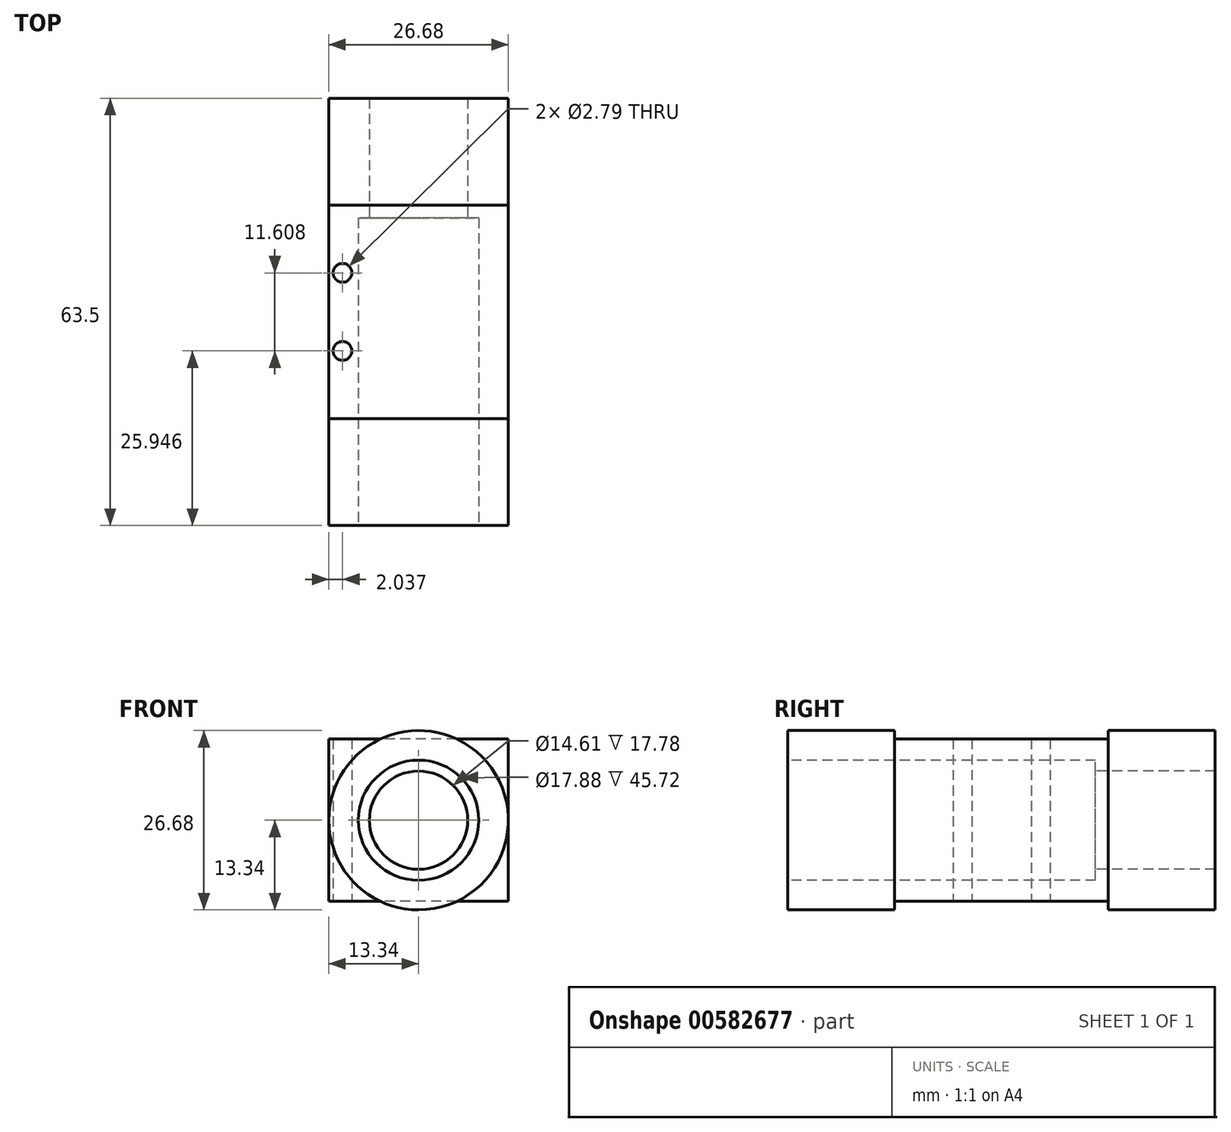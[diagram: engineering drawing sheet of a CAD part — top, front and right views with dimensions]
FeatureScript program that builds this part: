
annotation { "Feature Type Name" : "Feature", "Feature Type Description" : "" }
export const myFeature = defineFeature(function(context is Context, id is Id, definition is map)
    precondition{}
    {
        {
            var Q0;
            Q0=qCreatedBy(makeId("Front.planeOp"),FACE);
            cPlane(context, id + "F0", {"entities" : qUnion([Q0]), "cplaneType" : CPlaneType.OFFSET, "offset" : 31.75 * mm, "width" : 152.4 * mm, "height" : 152.4 * mm});
        }
        {
            var Q0;
            Q0=qCreatedBy(makeId("Front.planeOp"),FACE);
            cPlane(context, id + "F1", {"entities" : qUnion([Q0]), "cplaneType" : CPlaneType.OFFSET, "offset" : 31.75 * mm, "oppositeDirection" : true, "width" : 152.4 * mm, "height" : 152.4 * mm});
        }
        {
            var Q0;
            Q0=qCreatedBy(makeId("Top.planeOp"),FACE);
            cPlane(context, id + "F2", {"entities" : qUnion([Q0]), "cplaneType" : CPlaneType.OFFSET, "offset" : 13.33 * mm, "oppositeDirection" : true, "width" : 152.4 * mm, "height" : 152.4 * mm});
        }
        {
            var Q0;
            Q0=qCreatedBy(makeId("Front.planeOp"),FACE);
            cPlane(context, id + "F3", {"entities" : qUnion([Q0]), "cplaneType" : CPlaneType.OFFSET, "offset" : 15.88 * mm, "width" : 152.4 * mm, "height" : 152.4 * mm});
        }
        {
            var Q0;
            Q0=qCreatedBy(makeId("Front.planeOp"),FACE);
            cPlane(context, id + "F4", {"entities" : qUnion([Q0]), "cplaneType" : CPlaneType.OFFSET, "offset" : 15.88 * mm, "oppositeDirection" : true, "width" : 152.4 * mm, "height" : 152.4 * mm});
        }
        {
            var Q0;
            Q0=qCreatedBy(id+"F3.planeOp",FACE);
            var sketch = newSketch(context, id + "F5", { "sketchPlane" : qUnion([Q0])});
            skLineSegment(sketch, "E0.bottom", {"start": v(13.33, -13.33) * mm, "end": v(-13.34, -13.34) * mm});
            skLineSegment(sketch, "E0.top", {"start": v(13.34, 13.34) * mm, "end": v(-13.34, 13.33) * mm});
            skLineSegment(sketch, "E0.left", {"start": v(13.34, -13.33) * mm, "end": v(13.34, 13.34) * mm});
            skLineSegment(sketch, "E0.right", {"start": v(-13.34, -13.34) * mm, "end": v(-13.34, 13.33) * mm});
            skPoint(sketch, "E0.middle", {"position": v(0, 0) * mm});
            skSolve(sketch);
        }
        {
            var Q0;
            Q0=makeQuery(id+"F5.imprint","IMPRINT",FACE,{"disambiguationData":[TD([[makeQuery(id+"F5.imprint","IMPRINT",EDGE,{"derivedFrom":sQuery(id+"F5.wireOp",EDGE,"E0.bottom")}),-1.0]])]});
            extrude(context, id + "F6", {"entities" : qUnion([Q0]), "oppositeDirection" : true, "depth" : 31.75 * mm, "offsetDistance" : 25.4 * mm});
        }
        {
            var Q0;
            Q0=qCreatedBy(id+"F3.planeOp",FACE);
            var sketch = newSketch(context, id + "F7", { "sketchPlane" : qUnion([Q0])});
            skCircle(sketch, "E1", {"center": v(0, 0) * mm, "radius": 13.34 * mm});
            skSolve(sketch);
        }
        {
            var Q0;
            Q0=qCreatedBy(id+"F4.planeOp",FACE);
            var sketch = newSketch(context, id + "F8", { "sketchPlane" : qUnion([Q0])});
            skCircle(sketch, "E2", {"center": v(0, 0) * mm, "radius": 13.34 * mm});
            skSolve(sketch);
        }
        {
            var Q0;
            Q0=makeQuery(id+"F7.imprint","IMPRINT",FACE,{"disambiguationData":[TD([[makeQuery(id+"F7.imprint","IMPRINT",EDGE,{"derivedFrom":sQuery(id+"F7.wireOp",EDGE,"E1")}),1.0]])]});
            extrude(context, id + "F9", {"entities" : qUnion([Q0]), "operationType" : NewBodyOperationType.ADD, "depth" : 15.88 * mm, "offsetDistance" : 25.4 * mm});
        }
        {
            var Q0;
            Q0=makeQuery(id+"F8.imprint","IMPRINT",FACE,{"disambiguationData":[TD([[makeQuery(id+"F8.imprint","IMPRINT",EDGE,{"derivedFrom":sQuery(id+"F8.wireOp",EDGE,"E2")}),1.0]])]});
            extrude(context, id + "F10", {"entities" : qUnion([Q0]), "operationType" : NewBodyOperationType.ADD, "oppositeDirection" : true, "depth" : 15.88 * mm, "offsetDistance" : 25.4 * mm});
        }
        {
            var Q0;
            Q0=qCreatedBy(id+"F0.planeOp",FACE);
            var sketch = newSketch(context, id + "F11", { "sketchPlane" : qUnion([Q0])});
            skCircle(sketch, "E3", {"center": v(0, 0) * mm, "radius": 8.94 * mm});
            skSolve(sketch);
        }
        {
            var Q0;
            Q0=qCreatedBy(id+"F0.planeOp",FACE);
            var sketch = newSketch(context, id + "F12", { "sketchPlane" : qUnion([Q0])});
            skCircle(sketch, "E4", {"center": v(0, 0) * mm, "radius": 7.3 * mm});
            skSolve(sketch);
        }
        {
            var Q0;
            Q0=qCreatedBy(id+"F1.planeOp",FACE);
            var sketch = newSketch(context, id + "F13", { "sketchPlane" : qUnion([Q0])});
            skCircle(sketch, "E5", {"center": v(0, 0) * mm, "radius": 7.3 * mm});
            skSolve(sketch);
        }
        {
            var Q0;
            Q0 = qSketchRegion(id + "F12", true);
            extrude(context, id + "F14", {"entities" : qUnion([Q0]), "operationType" : NewBodyOperationType.REMOVE, "oppositeDirection" : true, "depth" : 63.5 * mm, "offsetDistance" : 25.4 * mm});
        }
        {
            var Q0;
            Q0=makeQuery(id+"F11.imprint","IMPRINT",FACE,{"disambiguationData":[TD([[makeQuery(id+"F11.imprint","IMPRINT",EDGE,{"derivedFrom":sQuery(id+"F11.wireOp",EDGE,"E3")}),1.0]])]});
            extrude(context, id + "F15", {"entities" : qUnion([Q0]), "operationType" : NewBodyOperationType.REMOVE, "oppositeDirection" : true, "depth" : 45.72 * mm, "offsetDistance" : 25.4 * mm});
        }
        {
            var Q0;
            Q0=makeQuery(id+"F13.imprint","IMPRINT",FACE,{"disambiguationData":[TD([[makeQuery(id+"F13.imprint","IMPRINT",EDGE,{"derivedFrom":sQuery(id+"F13.wireOp",EDGE,"E5")}),1.0]])]});
            extrude(context, id + "F16", {"entities" : qUnion([Q0]), "operationType" : NewBodyOperationType.REMOVE, "depth" : 63.5 * mm, "offsetDistance" : 25.4 * mm});
        }
        {
            var Q0;
            Q0=qCreatedBy(id+"F2.planeOp",FACE);
            var sketch = newSketch(context, id + "F17", { "sketchPlane" : qUnion([Q0])});
            skPoint(sketch, "E6", {"position": v(-11.3, -5.8) * mm});
            skPoint(sketch, "E7", {"position": v(-11.3, 5.8) * mm});
            skPoint(sketch, "E8", {"position": v(0, 5.8) * mm});
            skPoint(sketch, "E9", {"position": v(0, -5.8) * mm});
            skSolve(sketch);
        }
        {
            var Q0;
            Q0=sQuery(id+"F17.wireOp",VERTEX,"E7");
            var Q1;
            Q1=makeQuery(id+"F6.opExtrude","SWEPT_BODY",BODY,{"disambiguationData":[OSD([sQuery(id+"F5.wireOp",EDGE,"E0.bottom"),sQuery(id+"F5.wireOp",EDGE,"E0.top"),sQuery(id+"F5.wireOp",EDGE,"E0.left"),sQuery(id+"F5.wireOp",EDGE,"E0.right")])]});
            hole(context, id + "F18", {"style" : HoleStyle.SIMPLE, "endStyle" : HoleEndStyle.THROUGH, "oppositeDirection" : true, "holeDiameter" : 2.8 * mm, "majorDiameter" : 6.35 * mm, "isTappedThrough" : true, "tappedDepth" : 12.7 * mm, "tapClearance" : 3, "startFromSketch" : true, "locations" : qUnion([Q0]), "scope" : qUnion([Q1])});
        }
        {
            var Q0;
            Q0=sQuery(id+"F17.wireOp",VERTEX,"E6");
            var Q1;
            Q1=makeQuery(id+"F6.opExtrude","SWEPT_BODY",BODY,{"disambiguationData":[OSD([sQuery(id+"F5.wireOp",EDGE,"E0.bottom"),sQuery(id+"F5.wireOp",EDGE,"E0.top"),sQuery(id+"F5.wireOp",EDGE,"E0.left"),sQuery(id+"F5.wireOp",EDGE,"E0.right")])]});
            hole(context, id + "F19", {"style" : HoleStyle.SIMPLE, "endStyle" : HoleEndStyle.THROUGH, "oppositeDirection" : true, "holeDiameter" : 2.8 * mm, "majorDiameter" : 6.35 * mm, "isTappedThrough" : true, "tappedDepth" : 12.7 * mm, "tapClearance" : 3, "startFromSketch" : true, "locations" : qUnion([Q0]), "scope" : qUnion([Q1])});
        }
        {
            var Q0;
            Q0=makeQuery(id+"F6.opExtrude","SWEPT_FACE",FACE,{"disambiguationData":[OSD([sQuery(id+"F5.wireOp",EDGE,"E0.top")])]});
            extrude(context, id + "F20", {"entities" : qUnion([Q0]), "operationType" : NewBodyOperationType.REMOVE, "oppositeDirection" : true, "depth" : 1.27 * mm, "offsetDistance" : 25.4 * mm});
        }
        {
            var Q0;
            Q0=makeQuery(id+"F6.opExtrude","SWEPT_FACE",FACE,{"disambiguationData":[OSD([sQuery(id+"F5.wireOp",EDGE,"E0.bottom")])]});
            extrude(context, id + "F21", {"entities" : qUnion([Q0]), "operationType" : NewBodyOperationType.REMOVE, "oppositeDirection" : true, "depth" : 1.27 * mm, "offsetDistance" : 25.4 * mm});
        }
    });
